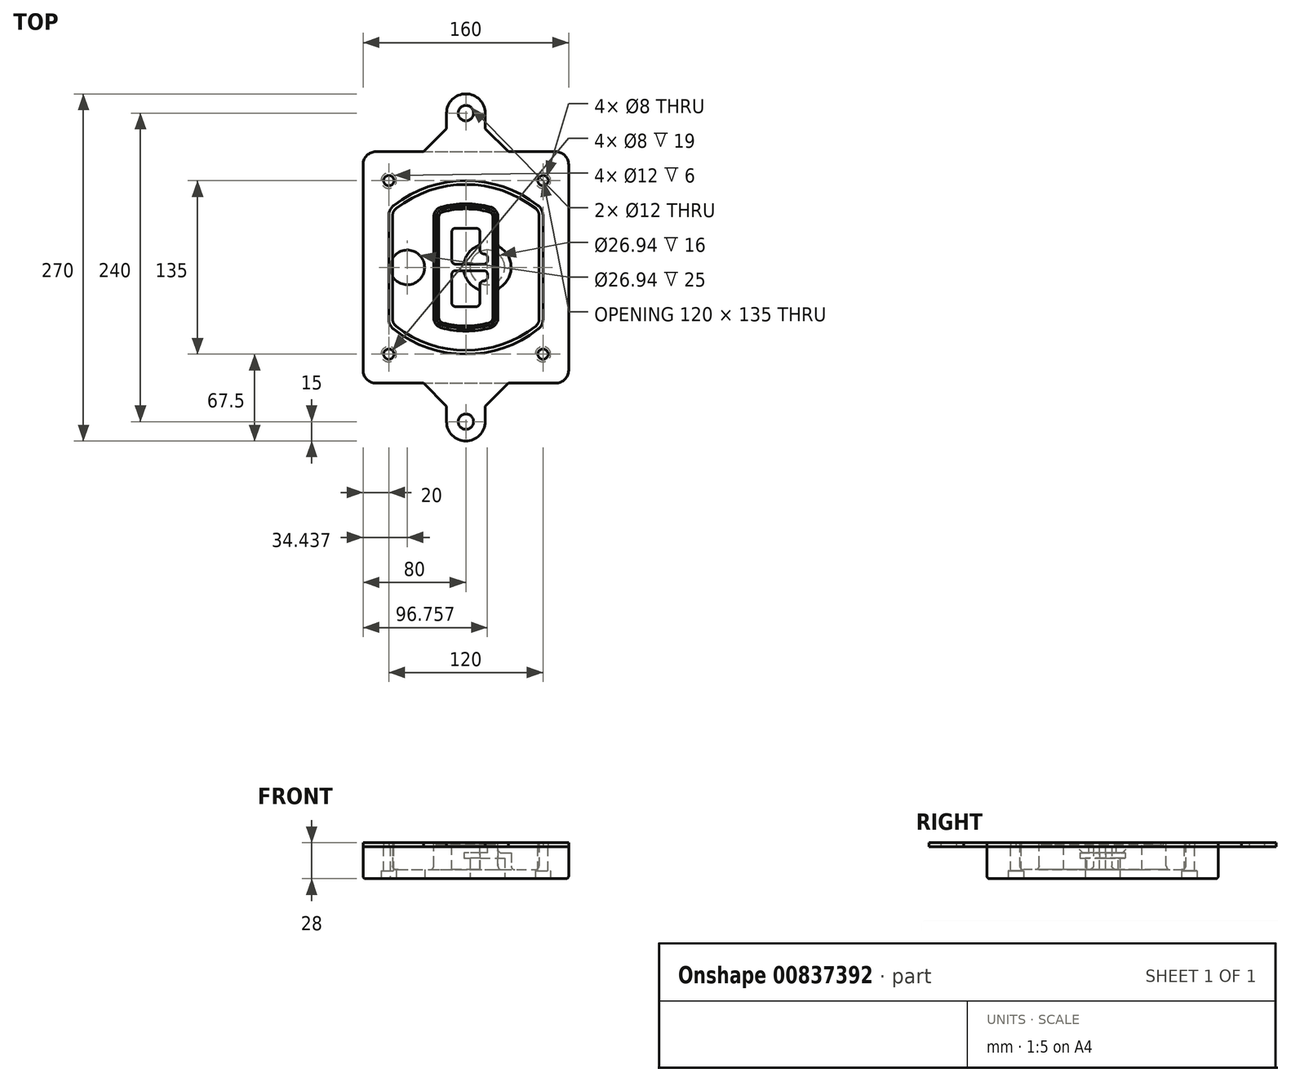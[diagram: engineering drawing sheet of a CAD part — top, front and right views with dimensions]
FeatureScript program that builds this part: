
annotation { "Feature Type Name" : "Feature", "Feature Type Description" : "" }
export const myFeature = defineFeature(function(context is Context, id is Id, definition is map)
    precondition{}
    {
        {
            var Q0;
            Q0=qCreatedBy(makeId("Top.planeOp"),FACE);
            var sketch = newSketch(context, id + "F0", { "sketchPlane" : qUnion([Q0])});
            skPoint(sketch, "E0.rect.middle", {"position": v(0, 0) * mm});
            skLineSegment(sketch, "E1.bottom", {"start": v(-70, -90) * mm, "end": v(70, -90) * mm});
            skLineSegment(sketch, "E1.top", {"start": v(-70, 90) * mm, "end": v(70, 90) * mm});
            skLineSegment(sketch, "E1.left", {"start": v(-80, -80) * mm, "end": v(-80, 80) * mm});
            skLineSegment(sketch, "E1.right", {"start": v(80, -80) * mm, "end": v(80, 80) * mm});
            skLineSegment(sketch, "E2", {"start": v(-80, 90) * mm, "end": v(80, -90) * mm, "construction": true});
            skLineSegment(sketch, "E3", {"start": v(80, 90) * mm, "end": v(-80, -90) * mm, "construction": true});
            skCircle(sketch, "E4", {"center": v(-60, 67.5) * mm, "radius": 4 * mm});
            skCircle(sketch, "E5", {"center": v(60, 67.5) * mm, "radius": 4 * mm});
            skCircle(sketch, "E6", {"center": v(60, -67.5) * mm, "radius": 4 * mm});
            skCircle(sketch, "E7", {"center": v(-60, -67.5) * mm, "radius": 4 * mm});
            skLineSegment(sketch, "E8", {"start": v(-60, 67.5) * mm, "end": v(60, 67.5) * mm, "construction": true});
            skLineSegment(sketch, "E9", {"start": v(60, 67.5) * mm, "end": v(60, -67.5) * mm, "construction": true});
            skLineSegment(sketch, "E10", {"start": v(60, -67.5) * mm, "end": v(-60, -67.5) * mm, "construction": true});
            skLineSegment(sketch, "E11", {"start": v(-60, -67.5) * mm, "end": v(-60, 67.5) * mm, "construction": true});
            skLineSegment(sketch, "E12", {"start": v(-60, 40.3) * mm, "end": v(-60, -40.3) * mm});
            skLineSegment(sketch, "E13", {"start": v(60, 40.3) * mm, "end": v(60, -40.3) * mm});
            skArc(sketch, "E14", {"start": v(56.15, 48.18) * mm, "mid": v(0, 67.5) * mm, "end": v(-56.15, 48.18) * mm});
            skArc(sketch, "E15", {"start": v(-56.15, -48.18) * mm, "mid": v(0, -67.5) * mm, "end": v(56.15, -48.18) * mm});
            skLineSegment(sketch, "E16", {"start": v(-60, 0) * mm, "end": v(60, 0) * mm, "construction": true});
            skPoint(sketch, "E17.visualSharp", {"position": v(-60, -45) * mm});
            skArc(sketch, "E17.filletArc", {"start": v(-60, -40.3) * mm, "mid": v(-58.99, -44.68) * mm, "end": v(-56.15, -48.18) * mm});
            skPoint(sketch, "E18.visualSharp", {"position": v(-60, 45) * mm});
            skArc(sketch, "E18.filletArc", {"start": v(-56.15, 48.18) * mm, "mid": v(-58.99, 44.68) * mm, "end": v(-60, 40.3) * mm});
            skPoint(sketch, "E19.visualSharp", {"position": v(60, 45) * mm});
            skArc(sketch, "E19.filletArc", {"start": v(60, 40.3) * mm, "mid": v(58.99, 44.68) * mm, "end": v(56.15, 48.18) * mm});
            skPoint(sketch, "E20.visualSharp", {"position": v(60, -45) * mm});
            skArc(sketch, "E20.filletArc", {"start": v(56.15, -48.18) * mm, "mid": v(58.99, -44.68) * mm, "end": v(60, -40.3) * mm});
            skPoint(sketch, "E21.visualSharp", {"position": v(-80, 90) * mm});
            skArc(sketch, "E21.filletArc", {"start": v(-70, 90) * mm, "mid": v(-77.07, 87.07) * mm, "end": v(-80, 80) * mm});
            skPoint(sketch, "E22.visualSharp", {"position": v(80, 90) * mm});
            skArc(sketch, "E22.filletArc", {"start": v(80, 80) * mm, "mid": v(77.07, 87.07) * mm, "end": v(70, 90) * mm});
            skPoint(sketch, "E23.visualSharp", {"position": v(80, -90) * mm});
            skArc(sketch, "E23.filletArc", {"start": v(70, -90) * mm, "mid": v(77.07, -87.07) * mm, "end": v(80, -80) * mm});
            skPoint(sketch, "E24.visualSharp", {"position": v(-80, -90) * mm});
            skArc(sketch, "E24.filletArc", {"start": v(-80, -80) * mm, "mid": v(-77.07, -87.07) * mm, "end": v(-70, -90) * mm});
            skArc(sketch, "E25.0", {"start": v(57, 40.3) * mm, "mid": v(56.3, 43.36) * mm, "end": v(54.3, 45.81) * mm});
            skLineSegment(sketch, "E25.1", {"start": v(57, 40.3) * mm, "end": v(57, -40.3) * mm});
            skArc(sketch, "E25.2", {"start": v(54.3, -45.81) * mm, "mid": v(56.3, -43.36) * mm, "end": v(57, -40.3) * mm});
            skArc(sketch, "E25.3", {"start": v(-54.3, -45.81) * mm, "mid": v(0, -64.5) * mm, "end": v(54.3, -45.81) * mm});
            skArc(sketch, "E25.4", {"start": v(-57, -40.3) * mm, "mid": v(-56.3, -43.36) * mm, "end": v(-54.3, -45.81) * mm});
            skArc(sketch, "E25.5", {"start": v(54.3, 45.81) * mm, "mid": v(0, 64.5) * mm, "end": v(-54.3, 45.81) * mm});
            skLineSegment(sketch, "E25.6", {"start": v(-57, 40.3) * mm, "end": v(-57, -40.3) * mm});
            skArc(sketch, "E25.7", {"start": v(-54.3, 45.81) * mm, "mid": v(-56.3, 43.36) * mm, "end": v(-57, 40.3) * mm});
            skArc(sketch, "E26.0", {"start": v(-58.62, 51.33) * mm, "mid": v(-62.58, 46.43) * mm, "end": v(-64, 40.3) * mm});
            skArc(sketch, "E26.1", {"start": v(58.62, 51.33) * mm, "mid": v(0, 71.5) * mm, "end": v(-58.62, 51.33) * mm});
            skArc(sketch, "E26.2", {"start": v(64, 40.3) * mm, "mid": v(62.58, 46.43) * mm, "end": v(58.62, 51.33) * mm});
            skLineSegment(sketch, "E26.3", {"start": v(64, 40.3) * mm, "end": v(64, -40.3) * mm});
            skArc(sketch, "E26.4", {"start": v(58.62, -51.33) * mm, "mid": v(62.58, -46.43) * mm, "end": v(64, -40.3) * mm});
            skLineSegment(sketch, "E26.5", {"start": v(-64, 40.3) * mm, "end": v(-64, -40.3) * mm});
            skArc(sketch, "E26.6", {"start": v(-58.62, -51.33) * mm, "mid": v(0, -71.5) * mm, "end": v(58.62, -51.33) * mm});
            skArc(sketch, "E26.7", {"start": v(-64, -40.3) * mm, "mid": v(-62.58, -46.43) * mm, "end": v(-58.62, -51.33) * mm});
            skSolve(sketch);
        }
        {
            var Q0;
            Q0=makeQuery(id+"F0.imprint","IMPRINT",FACE,{"disambiguationData":[TD([[makeQuery(id+"F0.imprint","IMPRINT",EDGE,{"derivedFrom":sQuery(id+"F0.wireOp",EDGE,"E1.bottom")}),1.0]])]});
            var Q1;
            Q1=makeQuery(id+"F0.imprint","IMPRINT",FACE,{"disambiguationData":[TD([[makeQuery(id+"F0.imprint","IMPRINT",EDGE,{"derivedFrom":sQuery(id+"F0.wireOp",EDGE,"E12")}),1.0]])]});
            var Q2;
            Q2=makeQuery(id+"F0.imprint","IMPRINT",FACE,{"disambiguationData":[TD([[makeQuery(id+"F0.imprint","IMPRINT",EDGE,{"derivedFrom":sQuery(id+"F0.wireOp",EDGE,"E25.0")}),1.0]])]});
            var Q3;
            Q3=makeQuery(id+"F0.imprint","IMPRINT",FACE,{"disambiguationData":[TD([[makeQuery(id+"F0.imprint","IMPRINT",EDGE,{"derivedFrom":sQuery(id+"F0.wireOp",EDGE,"E12")}),-1.0]])]});
            extrude(context, id + "F1", {"entities" : qUnion([Q0, Q1, Q2, Q3]), "oppositeDirection" : true, "depth" : 25 * mm});
        }
        {
            var Q0;
            Q0=makeQuery(id+"F0.imprint","IMPRINT",FACE,{"disambiguationData":[TD([[makeQuery(id+"F0.imprint","IMPRINT",EDGE,{"derivedFrom":sQuery(id+"F0.wireOp",EDGE,"E12")}),1.0]])]});
            extrude(context, id + "F2", {"entities" : qUnion([Q0]), "operationType" : NewBodyOperationType.ADD, "depth" : 3 * mm});
        }
        {
            var Q0;
            Q0=makeQuery(id+"F0.imprint","IMPRINT",FACE,{"disambiguationData":[TD([[makeQuery(id+"F0.imprint","IMPRINT",EDGE,{"derivedFrom":sQuery(id+"F0.wireOp",EDGE,"E25.0")}),1.0]])]});
            extrude(context, id + "F3", {"entities" : qUnion([Q0]), "operationType" : NewBodyOperationType.REMOVE, "oppositeDirection" : true, "depth" : 18 * mm});
        }
        {
            var Q0;
            Q0=makeQuery(id+"F2.opExtrude","CAP_FACE",FACE,{"disambiguationData":[OSD([sQuery(id+"F0.wireOp",EDGE,"E12"),sQuery(id+"F0.wireOp",EDGE,"E13"),sQuery(id+"F0.wireOp",EDGE,"E14"),sQuery(id+"F0.wireOp",EDGE,"E15"),sQuery(id+"F0.wireOp",EDGE,"E17.filletArc"),sQuery(id+"F0.wireOp",EDGE,"E18.filletArc"),sQuery(id+"F0.wireOp",EDGE,"E19.filletArc"),sQuery(id+"F0.wireOp",EDGE,"E20.filletArc"),sQuery(id+"F0.wireOp",EDGE,"E25.0"),sQuery(id+"F0.wireOp",EDGE,"E25.1"),sQuery(id+"F0.wireOp",EDGE,"E25.2"),sQuery(id+"F0.wireOp",EDGE,"E25.3"),sQuery(id+"F0.wireOp",EDGE,"E25.4"),sQuery(id+"F0.wireOp",EDGE,"E25.5"),sQuery(id+"F0.wireOp",EDGE,"E25.6"),sQuery(id+"F0.wireOp",EDGE,"E25.7")])],"isStart":false});
            var sketch = newSketch(context, id + "F4", { "sketchPlane" : qUnion([Q0])});
            skArc(sketch, "E27.0", {"start": v(-19.08, -46.97) * mm, "mid": v(0, -49.5) * mm, "end": v(19.08, -46.97) * mm});
            skArc(sketch, "E28.0", {"start": v(19.08, 46.97) * mm, "mid": v(0, 49.5) * mm, "end": v(-19.08, 46.97) * mm});
            skLineSegment(sketch, "E29", {"start": v(-25, 39.25) * mm, "end": v(-25, -39.25) * mm});
            skLineSegment(sketch, "E30", {"start": v(25, 39.25) * mm, "end": v(25, -39.25) * mm});
            skLineSegment(sketch, "E31", {"start": v(-25, 45.1) * mm, "end": v(25, 45.1) * mm, "construction": true});
            skLineSegment(sketch, "E32", {"start": v(-25, -45.1) * mm, "end": v(25, -45.1) * mm, "construction": true});
            skPoint(sketch, "E33.visualSharp", {"position": v(-25, 45.1) * mm});
            skArc(sketch, "E33.filletArc", {"start": v(-19.08, 46.97) * mm, "mid": v(-23.35, 44.11) * mm, "end": v(-25, 39.25) * mm});
            skPoint(sketch, "E34.visualSharp", {"position": v(25, 45.1) * mm});
            skArc(sketch, "E34.filletArc", {"start": v(25, 39.25) * mm, "mid": v(23.35, 44.11) * mm, "end": v(19.08, 46.97) * mm});
            skPoint(sketch, "E35.visualSharp", {"position": v(25, -45.1) * mm});
            skArc(sketch, "E35.filletArc", {"start": v(19.08, -46.97) * mm, "mid": v(23.35, -44.11) * mm, "end": v(25, -39.25) * mm});
            skPoint(sketch, "E36.visualSharp", {"position": v(-25, -45.1) * mm});
            skArc(sketch, "E36.filletArc", {"start": v(-25, -39.25) * mm, "mid": v(-23.35, -44.11) * mm, "end": v(-19.08, -46.97) * mm});
            skArc(sketch, "E37.0", {"start": v(54.3, 45.81) * mm, "mid": v(0, 64.5) * mm, "end": v(-54.3, 45.81) * mm});
            skArc(sketch, "E37.1", {"start": v(-54.3, 45.81) * mm, "mid": v(-56.3, 43.36) * mm, "end": v(-57, 40.3) * mm});
            skLineSegment(sketch, "E37.2", {"start": v(-57, 40.3) * mm, "end": v(-57, -40.3) * mm});
            skArc(sketch, "E37.3", {"start": v(-57, -40.3) * mm, "mid": v(-56.3, -43.36) * mm, "end": v(-54.3, -45.81) * mm});
            skArc(sketch, "E37.4", {"start": v(-54.3, -45.81) * mm, "mid": v(0, -64.5) * mm, "end": v(54.3, -45.81) * mm});
            skArc(sketch, "E37.5", {"start": v(54.3, -45.81) * mm, "mid": v(56.3, -43.36) * mm, "end": v(57, -40.3) * mm});
            skLineSegment(sketch, "E37.6", {"start": v(57, 40.3) * mm, "end": v(57, -40.3) * mm});
            skArc(sketch, "E37.7", {"start": v(57, 40.3) * mm, "mid": v(56.3, 43.36) * mm, "end": v(54.3, 45.81) * mm});
            skLineSegment(sketch, "E38.0", {"start": v(23, 39.25) * mm, "end": v(23, -39.25) * mm});
            skArc(sketch, "E38.1", {"start": v(18.56, -45.04) * mm, "mid": v(21.76, -42.9) * mm, "end": v(23, -39.25) * mm});
            skArc(sketch, "E38.2", {"start": v(-18.56, -45.04) * mm, "mid": v(0, -47.5) * mm, "end": v(18.56, -45.04) * mm});
            skArc(sketch, "E38.3", {"start": v(-23, -39.25) * mm, "mid": v(-21.76, -42.9) * mm, "end": v(-18.56, -45.04) * mm});
            skLineSegment(sketch, "E38.4", {"start": v(-23, 39.25) * mm, "end": v(-23, -39.25) * mm});
            skArc(sketch, "E38.5", {"start": v(23, 39.25) * mm, "mid": v(21.76, 42.9) * mm, "end": v(18.56, 45.04) * mm});
            skArc(sketch, "E38.6", {"start": v(-18.56, 45.04) * mm, "mid": v(-21.76, 42.9) * mm, "end": v(-23, 39.25) * mm});
            skArc(sketch, "E38.7", {"start": v(18.56, 45.04) * mm, "mid": v(0, 47.5) * mm, "end": v(-18.56, 45.04) * mm});
            skArc(sketch, "E39.0", {"start": v(21, 39.25) * mm, "mid": v(20.18, 41.68) * mm, "end": v(18.04, 43.1) * mm});
            skLineSegment(sketch, "E39.1", {"start": v(21, 39.25) * mm, "end": v(21, -39.25) * mm});
            skArc(sketch, "E39.2", {"start": v(18.04, -43.1) * mm, "mid": v(20.18, -41.68) * mm, "end": v(21, -39.25) * mm});
            skArc(sketch, "E39.3", {"start": v(-18.04, -43.1) * mm, "mid": v(0, -45.5) * mm, "end": v(18.04, -43.1) * mm});
            skArc(sketch, "E39.4", {"start": v(-21, -39.25) * mm, "mid": v(-20.18, -41.68) * mm, "end": v(-18.04, -43.1) * mm});
            skArc(sketch, "E39.5", {"start": v(18.04, 43.1) * mm, "mid": v(0, 45.5) * mm, "end": v(-18.04, 43.1) * mm});
            skLineSegment(sketch, "E39.6", {"start": v(-21, 39.25) * mm, "end": v(-21, -39.25) * mm});
            skArc(sketch, "E39.7", {"start": v(-18.04, 43.1) * mm, "mid": v(-20.18, 41.68) * mm, "end": v(-21, 39.25) * mm});
            skLineSegment(sketch, "E40", {"start": v(-25, 0) * mm, "end": v(25, 0) * mm, "construction": true});
            skLineSegment(sketch, "E41", {"start": v(-11, 5.5) * mm, "end": v(-11, 27.5) * mm});
            skLineSegment(sketch, "E42", {"start": v(-8, 30.5) * mm, "end": v(8, 30.5) * mm});
            skLineSegment(sketch, "E43", {"start": v(11, 27.5) * mm, "end": v(11, 13.5) * mm});
            skLineSegment(sketch, "E44", {"start": v(14, 10.5) * mm, "end": v(14, 10.5) * mm});
            skLineSegment(sketch, "E45", {"start": v(17, 7.5) * mm, "end": v(17, 5.5) * mm});
            skLineSegment(sketch, "E46", {"start": v(14, 2.5) * mm, "end": v(-8, 2.5) * mm});
            skPoint(sketch, "E47.visualSharp", {"position": v(-11, 30.5) * mm});
            skArc(sketch, "E47.filletArc", {"start": v(-8, 30.5) * mm, "mid": v(-10.12, 29.62) * mm, "end": v(-11, 27.5) * mm});
            skPoint(sketch, "E48.visualSharp", {"position": v(11, 30.5) * mm});
            skArc(sketch, "E48.filletArc", {"start": v(11, 27.5) * mm, "mid": v(10.12, 29.62) * mm, "end": v(8, 30.5) * mm});
            skPoint(sketch, "E49.visualSharp", {"position": v(11, 10.5) * mm});
            skArc(sketch, "E49.filletArc", {"start": v(11, 13.5) * mm, "mid": v(11.88, 11.38) * mm, "end": v(14, 10.5) * mm});
            skPoint(sketch, "E50.visualSharp", {"position": v(17, 10.5) * mm});
            skArc(sketch, "E50.filletArc", {"start": v(17, 7.5) * mm, "mid": v(16.12, 9.62) * mm, "end": v(14, 10.5) * mm});
            skPoint(sketch, "E51.visualSharp", {"position": v(17, 2.5) * mm});
            skArc(sketch, "E51.filletArc", {"start": v(14, 2.5) * mm, "mid": v(16.12, 3.38) * mm, "end": v(17, 5.5) * mm});
            skPoint(sketch, "E52.visualSharp", {"position": v(-11, 2.5) * mm});
            skArc(sketch, "E52.filletArc", {"start": v(-11, 5.5) * mm, "mid": v(-10.12, 3.38) * mm, "end": v(-8, 2.5) * mm});
            skLineSegment(sketch, "E53.0.MirrorCS", {"start": v(14, -2.5) * mm, "end": v(-8, -2.5) * mm});
            skArc(sketch, "E54.0.MirrorCS", {"start": v(-11, -5.5) * mm, "mid": v(-10.12, -3.38) * mm, "end": v(-8, -2.5) * mm});
            skLineSegment(sketch, "E55.0.MirrorCS", {"start": v(-11, -5.5) * mm, "end": v(-11, -27.5) * mm});
            skArc(sketch, "E56.0.MirrorCS", {"start": v(-8, -30.5) * mm, "mid": v(-10.12, -29.62) * mm, "end": v(-11, -27.5) * mm});
            skLineSegment(sketch, "E57.0.MirrorCS", {"start": v(-8, -30.5) * mm, "end": v(8, -30.5) * mm});
            skArc(sketch, "E58.0.MirrorCS", {"start": v(11, -27.5) * mm, "mid": v(10.12, -29.62) * mm, "end": v(8, -30.5) * mm});
            skLineSegment(sketch, "E59.0.MirrorCS", {"start": v(11, -27.5) * mm, "end": v(11, -13.5) * mm});
            skArc(sketch, "E60.0.MirrorCS", {"start": v(11, -13.5) * mm, "mid": v(11.88, -11.38) * mm, "end": v(14, -10.5) * mm});
            skArc(sketch, "E61.0.MirrorCS", {"start": v(17, -7.5) * mm, "mid": v(16.12, -9.62) * mm, "end": v(14, -10.5) * mm});
            skLineSegment(sketch, "E62.0.MirrorCS", {"start": v(17, -7.5) * mm, "end": v(17, -5.5) * mm});
            skArc(sketch, "E63.0.MirrorCS", {"start": v(14, -2.5) * mm, "mid": v(16.12, -3.38) * mm, "end": v(17, -5.5) * mm});
            skSolve(sketch);
        }
        {
            var Q0;
            Q0=makeQuery(id+"F4.imprint","IMPRINT",FACE,{"disambiguationData":[TD([[makeQuery(id+"F4.imprint","IMPRINT",EDGE,{"derivedFrom":sQuery(id+"F4.wireOp",EDGE,"E27.0")}),1.0]])]});
            var Q1;
            Q1=makeQuery(id+"F4.imprint","IMPRINT",FACE,{"disambiguationData":[TD([[makeQuery(id+"F4.imprint","IMPRINT",EDGE,{"derivedFrom":sQuery(id+"F4.wireOp",EDGE,"E38.0")}),-1.0]])]});
            var Q2;
            Q2=makeQuery(id+"F4.imprint","IMPRINT",FACE,{"disambiguationData":[TD([[makeQuery(id+"F4.imprint","IMPRINT",EDGE,{"derivedFrom":sQuery(id+"F4.wireOp",EDGE,"E39.0")}),1.0]])]});
            extrude(context, id + "F5", {"entities" : qUnion([Q0, Q1, Q2]), "operationType" : NewBodyOperationType.ADD, "endBound" : BoundingType.UP_TO_NEXT, "oppositeDirection" : true, "depth" : 25 * mm});
        }
        {
            var Q0;
            Q0=makeQuery(id+"F4.imprint","IMPRINT",FACE,{"disambiguationData":[TD([[makeQuery(id+"F4.imprint","IMPRINT",EDGE,{"derivedFrom":sQuery(id+"F4.wireOp",EDGE,"E38.0")}),-1.0]])]});
            extrude(context, id + "F6", {"entities" : qUnion([Q0]), "operationType" : NewBodyOperationType.REMOVE, "oppositeDirection" : true, "depth" : 2 * mm});
        }
        {
            var Q0;
            Q0=makeQuery(id+"F1.opExtrude","CAP_FACE",FACE,{"disambiguationData":[OSD([sQuery(id+"F0.wireOp",EDGE,"E1.bottom"),sQuery(id+"F0.wireOp",EDGE,"E1.top"),sQuery(id+"F0.wireOp",EDGE,"E1.left"),sQuery(id+"F0.wireOp",EDGE,"E1.right"),sQuery(id+"F0.wireOp",EDGE,"E4"),sQuery(id+"F0.wireOp",EDGE,"E5"),sQuery(id+"F0.wireOp",EDGE,"E6"),sQuery(id+"F0.wireOp",EDGE,"E7"),sQuery(id+"F0.wireOp",EDGE,"E21.filletArc"),sQuery(id+"F0.wireOp",EDGE,"E22.filletArc"),sQuery(id+"F0.wireOp",EDGE,"E23.filletArc"),sQuery(id+"F0.wireOp",EDGE,"E24.filletArc")])],"isStart":false});
            var sketch = newSketch(context, id + "F7", { "sketchPlane" : qUnion([Q0])});
            skCircle(sketch, "E64", {"center": v(16.76, 0) * mm, "radius": 13.47 * mm});
            skCircle(sketch, "E65", {"center": v(-45.56, 0) * mm, "radius": 13.47 * mm});
            skLineSegment(sketch, "E66", {"start": v(80, 0) * mm, "end": v(-80, 0) * mm});
            skCircle(sketch, "E67", {"center": v(16.76, 0) * mm, "radius": 18.47 * mm});
            skCircle(sketch, "E68", {"center": v(60, -67.5) * mm, "radius": 6 * mm});
            skCircle(sketch, "E69", {"center": v(-60, -67.5) * mm, "radius": 6 * mm});
            skCircle(sketch, "E70", {"center": v(-60, 67.5) * mm, "radius": 6 * mm});
            skCircle(sketch, "E71", {"center": v(60, 67.5) * mm, "radius": 6 * mm});
            skSolve(sketch);
        }
        {
            var Q0;
            {var subQ1=sQuery(id+"F7.wireOp",EDGE,"E66");var subQ4=sQuery(id+"F7.wireOp",EDGE,"E64");var subQ6=makeQuery(id+"F7.imprint","INTERSECT",VERTEX,{"disambiguationData":[OD(0.0)],"derivedFrom":[subQ4,subQ1]});Q0=makeQuery(id+"F7.imprint","IMPRINT",FACE,{"disambiguationData":[TD([[makeQuery(id+"F7.imprint","IMPRINT",EDGE,{"disambiguationData":[TD([[subQ6,-1.0]])],"derivedFrom":subQ4}),-1.0]])]});}
            var Q1;
            {var subQ0=sQuery(id+"F7.wireOp",EDGE,"E66");var subQ1=sQuery(id+"F7.wireOp",EDGE,"E64");var subQ3=makeQuery(id+"F7.imprint","INTERSECT",VERTEX,{"disambiguationData":[OD(0.0)],"derivedFrom":[subQ1,subQ0]});Q1=makeQuery(id+"F7.imprint","IMPRINT",FACE,{"disambiguationData":[TD([[makeQuery(id+"F7.imprint","IMPRINT",EDGE,{"disambiguationData":[TD([[subQ3,-1.0]])],"derivedFrom":subQ1}),1.0]])]});}
            var Q2;
            {var subQ0=sQuery(id+"F7.wireOp",EDGE,"E66");var subQ1=sQuery(id+"F7.wireOp",EDGE,"E64");var subQ3=makeQuery(id+"F7.imprint","INTERSECT",VERTEX,{"disambiguationData":[OD(0.0)],"derivedFrom":[subQ1,subQ0]});Q2=makeQuery(id+"F7.imprint","IMPRINT",FACE,{"disambiguationData":[TD([[makeQuery(id+"F7.imprint","IMPRINT",EDGE,{"disambiguationData":[TD([[subQ3,1.0]])],"derivedFrom":subQ1}),1.0]])]});}
            var Q3;
            {var subQ1=sQuery(id+"F7.wireOp",EDGE,"E66");var subQ4=sQuery(id+"F7.wireOp",EDGE,"E64");var subQ6=makeQuery(id+"F7.imprint","INTERSECT",VERTEX,{"disambiguationData":[OD(0.0)],"derivedFrom":[subQ4,subQ1]});Q3=makeQuery(id+"F7.imprint","IMPRINT",FACE,{"disambiguationData":[TD([[makeQuery(id+"F7.imprint","IMPRINT",EDGE,{"disambiguationData":[TD([[subQ6,1.0]])],"derivedFrom":subQ4}),-1.0]])]});}
            extrude(context, id + "F8", {"entities" : qUnion([Q0, Q1, Q2, Q3]), "operationType" : NewBodyOperationType.ADD, "oppositeDirection" : true, "depth" : 20 * mm});
        }
        {
            var Q0;
            {var subQ0=sQuery(id+"F7.wireOp",EDGE,"E66");var subQ1=sQuery(id+"F7.wireOp",EDGE,"E64");var subQ3=makeQuery(id+"F7.imprint","INTERSECT",VERTEX,{"disambiguationData":[OD(0.0)],"derivedFrom":[subQ1,subQ0]});Q0=makeQuery(id+"F7.imprint","IMPRINT",FACE,{"disambiguationData":[TD([[makeQuery(id+"F7.imprint","IMPRINT",EDGE,{"disambiguationData":[TD([[subQ3,-1.0]])],"derivedFrom":subQ1}),1.0]])]});}
            var Q1;
            {var subQ0=sQuery(id+"F7.wireOp",EDGE,"E66");var subQ1=sQuery(id+"F7.wireOp",EDGE,"E64");var subQ3=makeQuery(id+"F7.imprint","INTERSECT",VERTEX,{"disambiguationData":[OD(0.0)],"derivedFrom":[subQ1,subQ0]});Q1=makeQuery(id+"F7.imprint","IMPRINT",FACE,{"disambiguationData":[TD([[makeQuery(id+"F7.imprint","IMPRINT",EDGE,{"disambiguationData":[TD([[subQ3,1.0]])],"derivedFrom":subQ1}),1.0]])]});}
            extrude(context, id + "F9", {"entities" : qUnion([Q0, Q1]), "operationType" : NewBodyOperationType.REMOVE, "oppositeDirection" : true, "depth" : 16 * mm});
        }
        {
            var Q0;
            {var subQ0=sQuery(id+"F7.wireOp",EDGE,"E66");var subQ1=sQuery(id+"F7.wireOp",EDGE,"E65");var subQ3=makeQuery(id+"F7.imprint","INTERSECT",VERTEX,{"disambiguationData":[OD(0.0)],"derivedFrom":[subQ1,subQ0]});Q0=makeQuery(id+"F7.imprint","IMPRINT",FACE,{"disambiguationData":[TD([[makeQuery(id+"F7.imprint","IMPRINT",EDGE,{"disambiguationData":[TD([[subQ3,-1.0]])],"derivedFrom":subQ1}),1.0]])]});}
            var Q1;
            {var subQ0=sQuery(id+"F7.wireOp",EDGE,"E66");var subQ1=sQuery(id+"F7.wireOp",EDGE,"E65");var subQ3=makeQuery(id+"F7.imprint","INTERSECT",VERTEX,{"disambiguationData":[OD(0.0)],"derivedFrom":[subQ1,subQ0]});Q1=makeQuery(id+"F7.imprint","IMPRINT",FACE,{"disambiguationData":[TD([[makeQuery(id+"F7.imprint","IMPRINT",EDGE,{"disambiguationData":[TD([[subQ3,1.0]])],"derivedFrom":subQ1}),1.0]])]});}
            extrude(context, id + "F10", {"entities" : qUnion([Q0, Q1]), "operationType" : NewBodyOperationType.REMOVE, "oppositeDirection" : true, "depth" : 25 * mm});
        }
        {
            var Q0;
            Q0=makeQuery(id+"F7.imprint","IMPRINT",FACE,{"disambiguationData":[TD([[makeQuery(id+"F7.imprint","IMPRINT",EDGE,{"derivedFrom":sQuery(id+"F7.wireOp",EDGE,"E68")}),1.0]])]});
            var Q1;
            Q1=makeQuery(id+"F7.imprint","IMPRINT",FACE,{"disambiguationData":[TD([[makeQuery(id+"F7.imprint","IMPRINT",EDGE,{"derivedFrom":makeQuery(id+"F1.opExtrude","CAP_EDGE",EDGE,{"disambiguationData":[OSD([sQuery(id+"F0.wireOp",EDGE,"E5")])],"isStart":false})}),-1.0]])]});
            var Q2;
            Q2=makeQuery(id+"F7.imprint","IMPRINT",FACE,{"disambiguationData":[TD([[makeQuery(id+"F7.imprint","IMPRINT",EDGE,{"derivedFrom":sQuery(id+"F7.wireOp",EDGE,"E69")}),1.0]])]});
            var Q3;
            Q3=makeQuery(id+"F7.imprint","IMPRINT",FACE,{"disambiguationData":[TD([[makeQuery(id+"F7.imprint","IMPRINT",EDGE,{"derivedFrom":makeQuery(id+"F1.opExtrude","CAP_EDGE",EDGE,{"disambiguationData":[OSD([sQuery(id+"F0.wireOp",EDGE,"E4")])],"isStart":false})}),-1.0]])]});
            var Q4;
            Q4=makeQuery(id+"F7.imprint","IMPRINT",FACE,{"disambiguationData":[TD([[makeQuery(id+"F7.imprint","IMPRINT",EDGE,{"derivedFrom":sQuery(id+"F7.wireOp",EDGE,"E70")}),1.0]])]});
            var Q5;
            Q5=makeQuery(id+"F7.imprint","IMPRINT",FACE,{"disambiguationData":[TD([[makeQuery(id+"F7.imprint","IMPRINT",EDGE,{"derivedFrom":makeQuery(id+"F1.opExtrude","CAP_EDGE",EDGE,{"disambiguationData":[OSD([sQuery(id+"F0.wireOp",EDGE,"E7")])],"isStart":false})}),-1.0]])]});
            var Q6;
            Q6=makeQuery(id+"F7.imprint","IMPRINT",FACE,{"disambiguationData":[TD([[makeQuery(id+"F7.imprint","IMPRINT",EDGE,{"derivedFrom":sQuery(id+"F7.wireOp",EDGE,"E71")}),1.0]])]});
            var Q7;
            Q7=makeQuery(id+"F7.imprint","IMPRINT",FACE,{"disambiguationData":[TD([[makeQuery(id+"F7.imprint","IMPRINT",EDGE,{"derivedFrom":makeQuery(id+"F1.opExtrude","CAP_EDGE",EDGE,{"disambiguationData":[OSD([sQuery(id+"F0.wireOp",EDGE,"E6")])],"isStart":false})}),-1.0]])]});
            extrude(context, id + "F11", {"entities" : qUnion([Q0, Q1, Q2, Q3, Q4, Q5, Q6, Q7]), "operationType" : NewBodyOperationType.REMOVE, "oppositeDirection" : true, "depth" : 6 * mm});
        }
        {
            var Q0;
            Q0=makeQuery(id+"F9.boolean.opBoolean","COPY",FACE,{"derivedFrom":makeQuery(id+"F9.opExtrude","CAP_FACE",FACE,{"disambiguationData":[OSD([sQuery(id+"F7.wireOp",EDGE,"E64")])],"isStart":false})});
            var sketch = newSketch(context, id + "F12", { "sketchPlane" : qUnion([Q0])});
            skArc(sketch, "E72.0", {"start": v(11, 17.55) * mm, "mid": v(2.57, 11.82) * mm, "end": v(-1.54, 2.5) * mm});
            skArc(sketch, "E72.1", {"start": v(-1.54, -2.5) * mm, "mid": v(2.57, -11.82) * mm, "end": v(11, -17.55) * mm});
            skLineSegment(sketch, "E73", {"start": v(-1.54, -2.5) * mm, "end": v(14, -2.5) * mm});
            skLineSegment(sketch, "E74.0", {"start": v(14, 2.5) * mm, "end": v(-1.54, 2.5) * mm});
            skArc(sketch, "E74.1", {"start": v(14, 2.5) * mm, "mid": v(16.12, 3.38) * mm, "end": v(17, 5.5) * mm});
            skLineSegment(sketch, "E74.2", {"start": v(17, 7.5) * mm, "end": v(17, 5.5) * mm});
            skArc(sketch, "E74.3", {"start": v(17, 7.5) * mm, "mid": v(16.12, 9.62) * mm, "end": v(14, 10.5) * mm});
            skArc(sketch, "E74.4", {"start": v(11, 13.5) * mm, "mid": v(11.88, 11.38) * mm, "end": v(14, 10.5) * mm});
            skLineSegment(sketch, "E74.5", {"start": v(11, 17.55) * mm, "end": v(11, 13.5) * mm});
            skLineSegment(sketch, "E74.7", {"start": v(14, -2.5) * mm, "end": v(-1.54, -2.5) * mm});
            skArc(sketch, "E74.8", {"start": v(14, -2.5) * mm, "mid": v(16.12, -3.38) * mm, "end": v(17, -5.5) * mm});
            skLineSegment(sketch, "E74.9", {"start": v(17, -7.5) * mm, "end": v(17, -5.5) * mm});
            skArc(sketch, "E74.10", {"start": v(17, -7.5) * mm, "mid": v(16.12, -9.62) * mm, "end": v(14, -10.5) * mm});
            skArc(sketch, "E74.11", {"start": v(11, -13.5) * mm, "mid": v(11.88, -11.38) * mm, "end": v(14, -10.5) * mm});
            skLineSegment(sketch, "E74.12", {"start": v(11, -17.55) * mm, "end": v(11, -13.5) * mm});
            skPoint(sketch, "E75.orphan", {"position": v(11, -27.5) * mm});
            skPoint(sketch, "E76.orphan", {"position": v(-8, -2.5) * mm});
            skPoint(sketch, "E77.orphan", {"position": v(-8, 2.5) * mm});
            skPoint(sketch, "E78.orphan", {"position": v(11, 27.5) * mm});
            skSolve(sketch);
        }
        {
            var Q0;
            {var subQ7=sQuery(id+"F12.wireOp",EDGE,"E72.0");var subQ14=sQuery(id+"F12.wireOp",EDGE,"E72.1");var subQ16=sQuery(id+"F12.wireOp",EDGE,"E74.1");var subQ18=sQuery(id+"F12.wireOp",EDGE,"E74.8");Q0=qUnion([makeQuery(id+"F12.imprint","IMPRINT",FACE,{"disambiguationData":[TD([[makeQuery(id+"F12.imprint","IMPRINT",EDGE,{"derivedFrom":subQ7}),1.0]])]}),makeQuery(id+"F12.imprint","IMPRINT",FACE,{"disambiguationData":[TD([[makeQuery(id+"F12.imprint","IMPRINT",EDGE,{"derivedFrom":subQ14}),1.0]])]}),makeQuery(id+"F12.imprint","IMPRINT",FACE,{"disambiguationData":[TD([[makeQuery(id+"F12.imprint","IMPRINT",EDGE,{"derivedFrom":subQ16}),1.0]])]}),makeQuery(id+"F12.imprint","IMPRINT",FACE,{"disambiguationData":[TD([[makeQuery(id+"F12.imprint","IMPRINT",EDGE,{"derivedFrom":subQ18}),-1.0]])]})]);}
            var Q1;
            Q1=makeQuery(id+"F5.boolean.opBoolean","SPLIT",FACE,{"disambiguationData":[TD([makeQuery(id+"F5.opExtrude","SWEPT_FACE",FACE,{"disambiguationData":[OSD([sQuery(id+"F4.wireOp",EDGE,"E41")])]})])],"derivedFrom":makeQuery(id+"F3.boolean.opBoolean","COPY",FACE,{"derivedFrom":makeQuery(id+"F3.opExtrude","CAP_FACE",FACE,{"disambiguationData":[OSD([sQuery(id+"F0.wireOp",EDGE,"E25.0"),sQuery(id+"F0.wireOp",EDGE,"E25.1"),sQuery(id+"F0.wireOp",EDGE,"E25.2"),sQuery(id+"F0.wireOp",EDGE,"E25.3"),sQuery(id+"F0.wireOp",EDGE,"E25.4"),sQuery(id+"F0.wireOp",EDGE,"E25.5"),sQuery(id+"F0.wireOp",EDGE,"E25.6"),sQuery(id+"F0.wireOp",EDGE,"E25.7")])],"isStart":false})})});
            extrude(context, id + "F13", {"entities" : qUnion([Q0]), "operationType" : NewBodyOperationType.REMOVE, "endBound" : BoundingType.UP_TO_SURFACE, "endBoundEntityFace" : qUnion([Q1]), "depth" : 25 * mm});
        }
        {
            var Q0;
            Q0=makeQuery(id+"F3.boolean.opBoolean","COPY",EDGE,{"derivedFrom":makeQuery(id+"F3.opExtrude","CAP_EDGE",EDGE,{"disambiguationData":[OSD([sQuery(id+"F0.wireOp",EDGE,"E25.6")])],"isStart":false})});
            var Q1;
            Q1=makeQuery(id+"F8.boolean.opBoolean","INTERSECT",EDGE,{"derivedFrom":[makeQuery(id+"F5.opExtrude","SWEPT_FACE",FACE,{"disambiguationData":[OSD([sQuery(id+"F4.wireOp",EDGE,"E30")])]}),makeQuery(id+"F8.opExtrude","CAP_FACE",FACE,{"disambiguationData":[OSD([sQuery(id+"F7.wireOp",EDGE,"E67")])],"isStart":false})]});
            var Q2;
            Q2=makeQuery(id+"F8.boolean.opBoolean","INTERSECT",EDGE,{"disambiguationData":[OD(1.0)],"derivedFrom":[makeQuery(id+"F5.opExtrude","SWEPT_FACE",FACE,{"disambiguationData":[OSD([sQuery(id+"F4.wireOp",EDGE,"E30")])]}),makeQuery(id+"F8.opExtrude","SWEPT_FACE",FACE,{"disambiguationData":[OSD([sQuery(id+"F7.wireOp",EDGE,"E67")])]})]});
            var Q3;
            {var subQ0=sQuery(id+"F4.wireOp",EDGE,"E30");Q3=makeQuery(id+"F8.boolean.opBoolean","SPLIT",EDGE,{"disambiguationData":[TD([makeQuery(id+"F5.opExtrude","SWEPT_FACE",FACE,{"disambiguationData":[OSD([sQuery(id+"F4.wireOp",EDGE,"E35.filletArc")])]})])],"derivedFrom":makeQuery(id+"F5.opExtrude","CAP_EDGE",EDGE,{"disambiguationData":[OSD([subQ0])],"isStart":false})});}
            var Q4;
            {var subQ0=sQuery(id+"F0.wireOp",EDGE,"E25.7");var subQ1=sQuery(id+"F0.wireOp",EDGE,"E25.1");var subQ2=sQuery(id+"F0.wireOp",EDGE,"E25.6");var subQ3=sQuery(id+"F0.wireOp",EDGE,"E25.5");var subQ4=sQuery(id+"F0.wireOp",EDGE,"E25.4");var subQ5=sQuery(id+"F0.wireOp",EDGE,"E25.0");var subQ6=sQuery(id+"F0.wireOp",EDGE,"E25.2");var subQ7=sQuery(id+"F0.wireOp",EDGE,"E25.3");Q4=makeQuery(id+"F8.boolean.opBoolean","INTERSECT",EDGE,{"derivedFrom":[makeQuery(id+"F5.boolean.opBoolean","SPLIT",FACE,{"disambiguationData":[TD([makeQuery(id+"F2.opExtrude","SWEPT_FACE",FACE,{"disambiguationData":[OSD([subQ5])]})])],"derivedFrom":makeQuery(id+"F3.boolean.opBoolean","COPY",FACE,{"derivedFrom":makeQuery(id+"F3.opExtrude","CAP_FACE",FACE,{"disambiguationData":[OSD([subQ5,subQ1,subQ6,subQ7,subQ4,subQ3,subQ2,subQ0])],"isStart":false})})}),makeQuery(id+"F8.opExtrude","SWEPT_FACE",FACE,{"disambiguationData":[OSD([sQuery(id+"F7.wireOp",EDGE,"E67")])]})]});}
            var Q5;
            Q5=makeQuery(id+"F8.boolean.opBoolean","INTERSECT",EDGE,{"disambiguationData":[OD(0.0)],"derivedFrom":[makeQuery(id+"F5.opExtrude","SWEPT_FACE",FACE,{"disambiguationData":[OSD([sQuery(id+"F4.wireOp",EDGE,"E30")])]}),makeQuery(id+"F8.opExtrude","SWEPT_FACE",FACE,{"disambiguationData":[OSD([sQuery(id+"F7.wireOp",EDGE,"E67")])]})]});
            fillet(context, id + "F14", {"entities" : qUnion([Q0, Q1, Q2, Q3, Q4, Q5]), "radius" : 3 * mm, "tangentPropagation" : true, "allowEdgeOverflow" : false});
        }
        {
            var Q0;
            Q0=makeQuery(id+"F1.opExtrude","CAP_EDGE",EDGE,{"disambiguationData":[OSD([sQuery(id+"F0.wireOp",EDGE,"E1.bottom")])],"isStart":false});
            fillet(context, id + "F15", {"entities" : qUnion([Q0]), "radius" : 2 * mm, "tangentPropagation" : true, "allowEdgeOverflow" : false});
        }
        {
            var Q0;
            {var subQ0=sQuery(id+"F0.wireOp",EDGE,"E21.filletArc");var subQ1=sQuery(id+"F0.wireOp",EDGE,"E7");var subQ2=sQuery(id+"F0.wireOp",EDGE,"E6");var subQ3=sQuery(id+"F0.wireOp",EDGE,"E5");var subQ4=sQuery(id+"F0.wireOp",EDGE,"E4");var subQ5=sQuery(id+"F0.wireOp",EDGE,"E22.filletArc");var subQ6=sQuery(id+"F0.wireOp",EDGE,"E1.bottom");var subQ7=sQuery(id+"F0.wireOp",EDGE,"E1.right");var subQ8=sQuery(id+"F0.wireOp",EDGE,"E1.top");var subQ9=sQuery(id+"F0.wireOp",EDGE,"E1.left");var subQ10=sQuery(id+"F0.wireOp",EDGE,"E23.filletArc");var subQ11=sQuery(id+"F0.wireOp",EDGE,"E24.filletArc");Q0=makeQuery(id+"F2.boolean.opBoolean","SPLIT",FACE,{"disambiguationData":[TD([makeQuery(id+"F1.opExtrude","SWEPT_FACE",FACE,{"disambiguationData":[OSD([subQ6])]})])],"derivedFrom":makeQuery(id+"F1.opExtrude","CAP_FACE",FACE,{"disambiguationData":[OSD([subQ6,subQ8,subQ9,subQ7,subQ4,subQ3,subQ2,subQ1,subQ0,subQ5,subQ10,subQ11])],"isStart":true})});}
            var sketch = newSketch(context, id + "F16", { "sketchPlane" : qUnion([Q0])});
            skLineSegment(sketch, "E79", {"start": v(-33, 90) * mm, "end": v(-15, 108) * mm});
            skLineSegment(sketch, "E80", {"start": v(-15, 108) * mm, "end": v(-15, 120) * mm});
            skLineSegment(sketch, "E81", {"start": v(33, 90) * mm, "end": v(15, 108) * mm});
            skLineSegment(sketch, "E82", {"start": v(15, 108) * mm, "end": v(15, 120) * mm});
            skCircle(sketch, "E83", {"center": v(0, 120) * mm, "radius": 6 * mm});
            skArc(sketch, "E84", {"start": v(15, 120) * mm, "mid": v(0, 135) * mm, "end": v(-15, 120) * mm});
            skLineSegment(sketch, "E85", {"start": v(-80, 0) * mm, "end": v(80, 0) * mm, "construction": true});
            skLineSegment(sketch, "E86.MirrorCS", {"start": v(33, -90) * mm, "end": v(15, -108) * mm});
            skLineSegment(sketch, "E87.MirrorCS", {"start": v(15, -108) * mm, "end": v(15, -120) * mm});
            skLineSegment(sketch, "E88.MirrorCS", {"start": v(-33, -90) * mm, "end": v(-15, -108) * mm});
            skArc(sketch, "E89.MirrorCS", {"start": v(15, -120) * mm, "mid": v(0, -135) * mm, "end": v(-15, -120) * mm});
            skLineSegment(sketch, "E90.MirrorCS", {"start": v(-15, -108) * mm, "end": v(-15, -120) * mm});
            skCircle(sketch, "E91.MirrorC", {"center": v(0, -120) * mm, "radius": 6 * mm});
            skSolve(sketch);
        }
        {
            var Q0;
            {var subQ1=sQuery(id+"F16.wireOp",EDGE,"E79");Q0=makeQuery(id+"F16.imprint","IMPRINT",FACE,{"disambiguationData":[TD([[makeQuery(id+"F16.imprint","IMPRINT",EDGE,{"derivedFrom":subQ1}),-1.0]])]});}
            var Q1;
            Q1=makeQuery(id+"F16.imprint","IMPRINT",FACE,{"disambiguationData":[TD([[makeQuery(id+"F16.imprint","IMPRINT",EDGE,{"derivedFrom":makeQuery(id+"F1.opExtrude","CAP_EDGE",EDGE,{"disambiguationData":[OSD([sQuery(id+"F0.wireOp",EDGE,"E1.left")])],"isStart":true})}),-1.0]])]});
            var Q2;
            {var subQ1=sQuery(id+"F16.wireOp",EDGE,"E86.MirrorCS");Q2=makeQuery(id+"F16.imprint","IMPRINT",FACE,{"disambiguationData":[TD([[makeQuery(id+"F16.imprint","IMPRINT",EDGE,{"derivedFrom":subQ1}),-1.0]])]});}
            var Q3;
            Q3=makeQuery(id+"F2.opExtrude","CAP_FACE",FACE,{"disambiguationData":[OSD([sQuery(id+"F0.wireOp",EDGE,"E12"),sQuery(id+"F0.wireOp",EDGE,"E13"),sQuery(id+"F0.wireOp",EDGE,"E14"),sQuery(id+"F0.wireOp",EDGE,"E15"),sQuery(id+"F0.wireOp",EDGE,"E17.filletArc"),sQuery(id+"F0.wireOp",EDGE,"E18.filletArc"),sQuery(id+"F0.wireOp",EDGE,"E19.filletArc"),sQuery(id+"F0.wireOp",EDGE,"E20.filletArc"),sQuery(id+"F0.wireOp",EDGE,"E25.0"),sQuery(id+"F0.wireOp",EDGE,"E25.1"),sQuery(id+"F0.wireOp",EDGE,"E25.2"),sQuery(id+"F0.wireOp",EDGE,"E25.3"),sQuery(id+"F0.wireOp",EDGE,"E25.4"),sQuery(id+"F0.wireOp",EDGE,"E25.5"),sQuery(id+"F0.wireOp",EDGE,"E25.6"),sQuery(id+"F0.wireOp",EDGE,"E25.7")])],"isStart":false});
            extrude(context, id + "F17", {"entities" : qUnion([Q0, Q1, Q2]), "endBound" : BoundingType.UP_TO_SURFACE, "depth" : 25 * mm, "endBoundEntityFace" : qUnion([Q3]), "offsetDistance" : 25 * mm});
        }
    });
